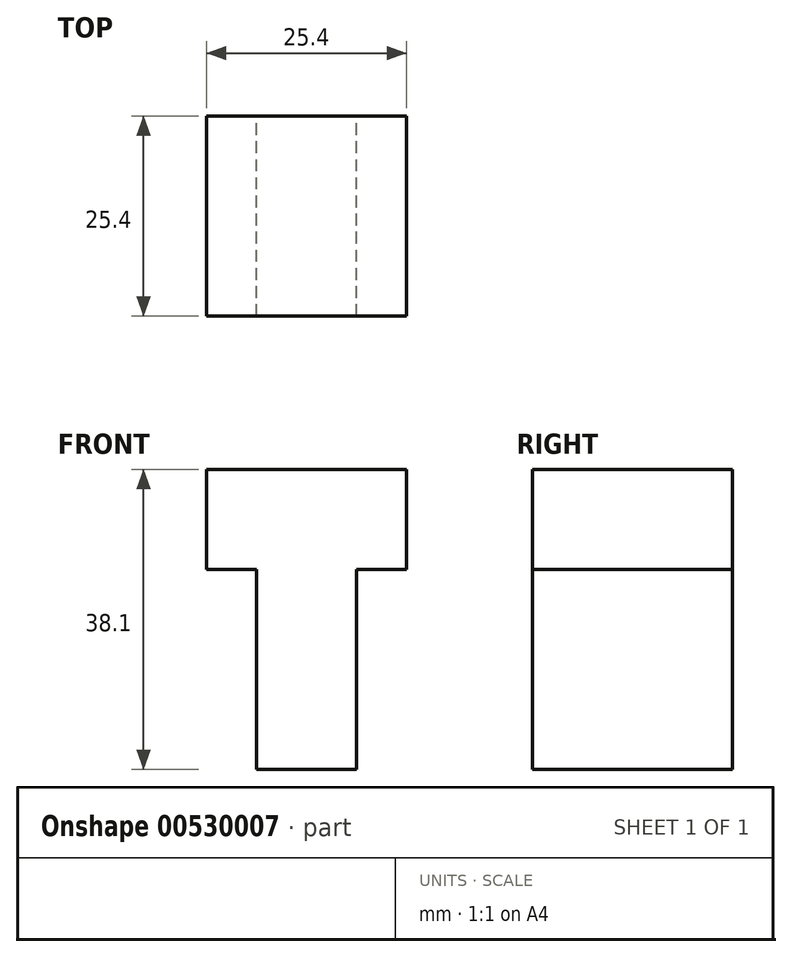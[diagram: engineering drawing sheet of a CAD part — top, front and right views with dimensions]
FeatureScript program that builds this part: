
annotation { "Feature Type Name" : "Feature", "Feature Type Description" : "" }
export const myFeature = defineFeature(function(context is Context, id is Id, definition is map)
    precondition{}
    {
        {
            var Q0;
            Q0=qCreatedBy(makeId("Front.planeOp"),FACE);
            var sketch = newSketch(context, id + "F0", { "sketchPlane" : qUnion([Q0])});
            skLineSegment(sketch, "E0", {"start": v(-71.96, 52.55) * mm, "end": v(-46.56, 52.55) * mm});
            skLineSegment(sketch, "E1", {"start": v(-71.96, 52.55) * mm, "end": v(-71.96, 39.85) * mm});
            skLineSegment(sketch, "E2", {"start": v(-71.96, 39.85) * mm, "end": v(-65.6, 39.85) * mm});
            skLineSegment(sketch, "E3", {"start": v(-65.6, 39.85) * mm, "end": v(-65.6, 14.45) * mm});
            skLineSegment(sketch, "E4", {"start": v(-65.6, 14.45) * mm, "end": v(-52.9, 14.45) * mm});
            skLineSegment(sketch, "E5", {"start": v(-52.9, 14.45) * mm, "end": v(-52.9, 39.85) * mm});
            skLineSegment(sketch, "E6", {"start": v(-52.9, 39.85) * mm, "end": v(-46.56, 39.85) * mm});
            skLineSegment(sketch, "E7", {"start": v(-46.56, 52.55) * mm, "end": v(-46.56, 39.85) * mm});
            skSolve(sketch);
        }
        {
            var Q0;
            Q0=makeQuery(id+"F0.imprint","IMPRINT",FACE,{"disambiguationData":[TD([[makeQuery(id+"F0.imprint","IMPRINT",EDGE,{"derivedFrom":sQuery(id+"F0.wireOp",EDGE,"E0")}),-1.0]])]});
            extrude(context, id + "F1", {"entities" : qUnion([Q0]), "depth" : 25.4 * mm, "offsetDistance" : 25.4 * mm});
        }
    });
